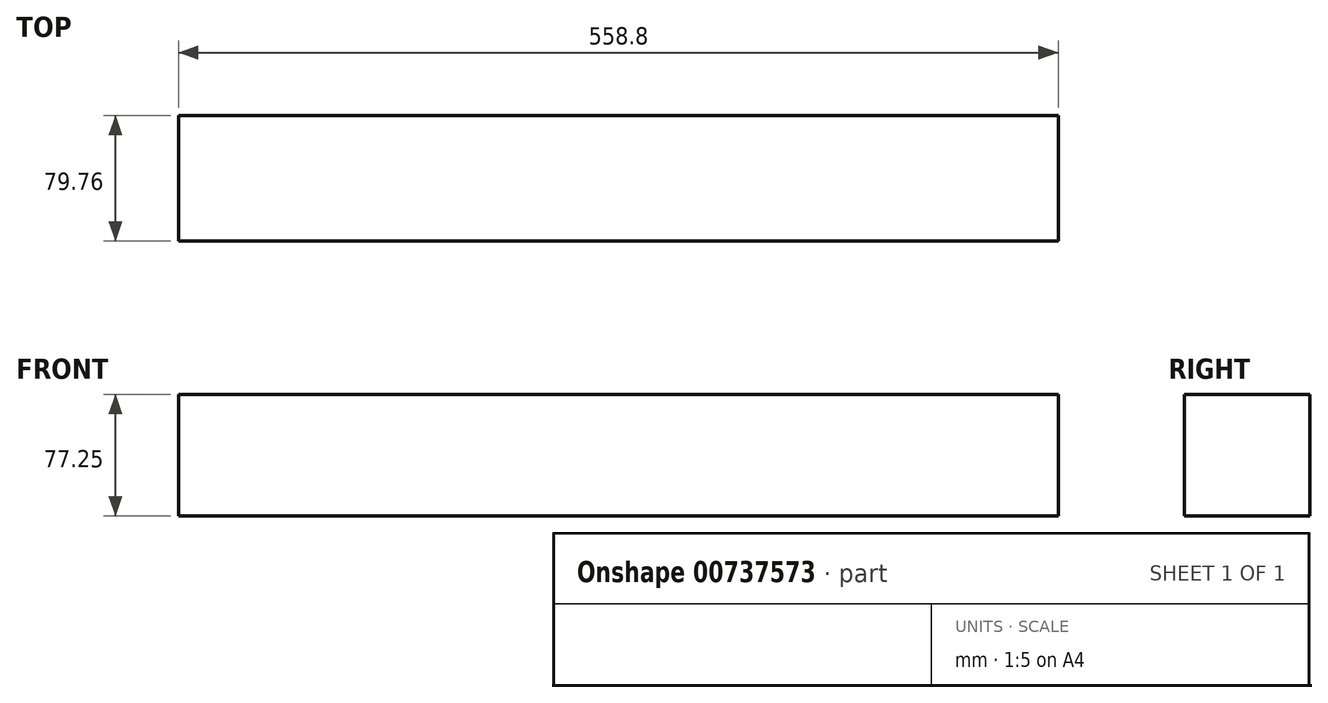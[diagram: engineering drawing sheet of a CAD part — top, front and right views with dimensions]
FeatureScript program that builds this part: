
annotation { "Feature Type Name" : "Feature", "Feature Type Description" : "" }
export const myFeature = defineFeature(function(context is Context, id is Id, definition is map)
    precondition{}
    {
        {
            var Q0;
            Q0=qCreatedBy(makeId("Right.planeOp"),FACE);
            var sketch = newSketch(context, id + "F0", { "sketchPlane" : qUnion([Q0])});
            skLineSegment(sketch, "E0.bottom", {"start": v(38.12, 40.13) * mm, "end": v(-41.64, 40.13) * mm});
            skLineSegment(sketch, "E0.top", {"start": v(38.12, -37.12) * mm, "end": v(-41.64, -37.12) * mm});
            skLineSegment(sketch, "E0.left", {"start": v(38.12, 40.13) * mm, "end": v(38.12, -37.12) * mm});
            skLineSegment(sketch, "E0.right", {"start": v(-41.64, 40.13) * mm, "end": v(-41.64, -37.12) * mm});
            skSolve(sketch);
        }
        {
            var Q0;
            Q0 = qSketchRegion(id + "F0", true);
            extrude(context, id + "F1", {"entities" : qUnion([Q0]), "oppositeDirection" : true, "depth" : 279.4 * mm, "offsetDistance" : 25.4 * mm});
        }
        {
            var Q0;
            Q0=makeQuery(id+"F1.opExtrude","CAP_FACE",FACE,{"disambiguationData":[OSD([sQuery(id+"F0.wireOp",EDGE,"E0.bottom"),sQuery(id+"F0.wireOp",EDGE,"E0.top"),sQuery(id+"F0.wireOp",EDGE,"E0.left"),sQuery(id+"F0.wireOp",EDGE,"E0.right")])],"isStart":true});
            extrude(context, id + "F2", {"entities" : qUnion([Q0]), "operationType" : NewBodyOperationType.ADD, "depth" : 279.4 * mm, "offsetDistance" : 25.4 * mm});
        }
    });
